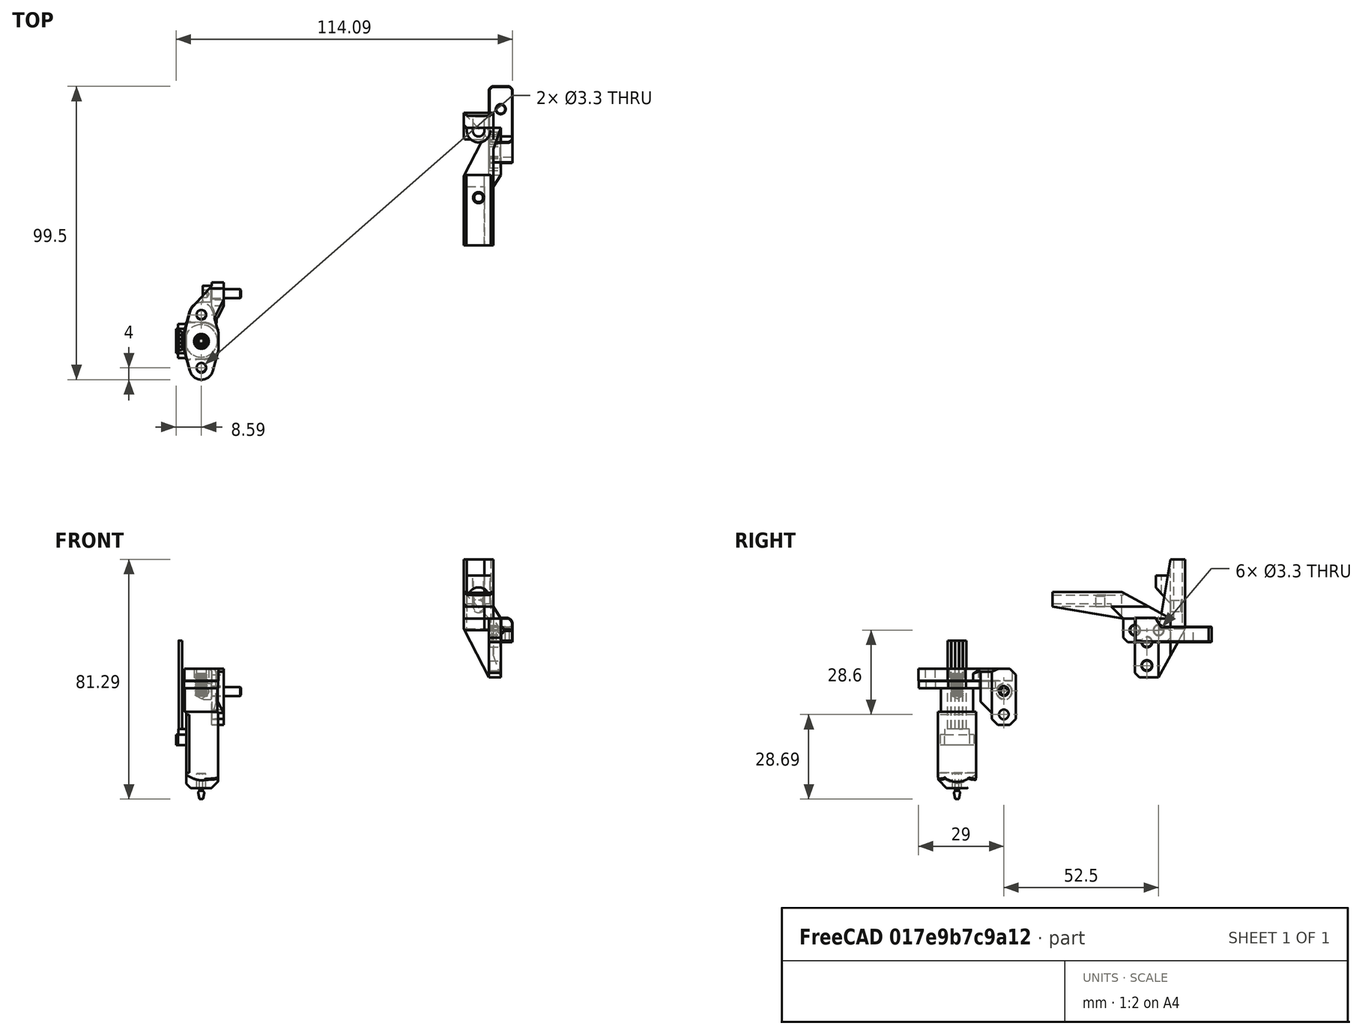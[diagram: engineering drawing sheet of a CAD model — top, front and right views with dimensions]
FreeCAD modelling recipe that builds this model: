
FCSTD DOCUMENT  (FreeCAD 0.19R24291 (Git))
Label: probe-mount-GXH8B
License: Other
LicenseURL: GPL3
objects: Part::Chamfer×18, Part::Box×14, Part::Cut×11, Part::Cylinder×5, Part::MultiFuse×5, Part::Feature×4, Part::FeaturePython×2, Part::Fillet×1, App::Part×1, Part::Refine×1
note: 61 computed .brp shape members not serialized (recipe doc carries the construction recipe); baked Part::Feature solids carry a one-line shape summary decoded from their .brp

FEATURE [Part::Box] Box  label="Cube"
  AttacherType = Attacher::AttachEngine3D
  Height = 8.2
  Length = 8
  Width = 9
FEATURE [Part::Box] Box001  label="Cube001"
  AttacherType = Attacher::AttachEngine3D
  Height = 5.2
  Length = 8
  Placement = pos=(0,8,0) rot=(0,0,1;0rad)
  Width = 18
FEATURE [Part::Box] Box002  label="Cube002"
  AttacherType = Attacher::AttachEngine3D
  Height = 0.2
  Length = 8
  Width = 2
FEATURE [Part::Cylinder] Cylinder
  Angle = 360
  AttacherType = Attacher::AttachEngine3D
  Height = 10
  Placement = pos=(4,18.25,0) rot=(0,0,1;0rad)
  Radius = 1.5
FEATURE [Part::Cylinder] Cylinder001
  Angle = 360
  AttacherType = Attacher::AttachEngine3D
  Height = 10
  Placement = pos=(4,0.25,4) rot=(1,0,0;1.5708rad)
  Radius = 1
FEATURE [Part::Box] Box003  label="Cube003"
  AttacherType = Attacher::AttachEngine3D
  Height = 2
  Length = 0.4
  Placement = pos=(3.8,0,0.5) rot=(0,0,1;0rad)
  Width = 0.25
FEATURE [Part::Box] Box004  label="Cube004"
  AttacherType = Attacher::AttachEngine3D
  Height = 2
  Length = 0.4
  Placement = pos=(3.8,0,5.5) rot=(0,0,1;0rad)
  Width = 0.25
FEATURE [Part::MultiFuse] Fusion001
  Shapes = -> [Box003,Box004]
FEATURE [Part::Feature] Fusion001001
  Placement = pos=(-1.8e-15,0,8) rot=(0,1,0;1.5708rad)
  shape: bbox 7 x 0.25 x 0.4 mm, 12 faces, 2 solids (baked)
FEATURE [Part::MultiFuse] Fusion001002
  Shapes = -> [Fusion001,Fusion001001]
FEATURE [Part::Cylinder] Cylinder002
  Angle = 360
  AttacherType = Attacher::AttachEngine3D
  Height = 10
  Placement = pos=(-1e-15,0,4) rot=(0,1,0;1.5708rad)
  Radius = 1.65
FEATURE [Part::Cylinder] Cylinder003
  Angle = 360
  AttacherType = Attacher::AttachEngine3D
  Height = 10
  Placement = pos=(-1e-15,8,4) rot=(0,1,0;1.5708rad)
  Radius = 1.65
FEATURE [Part::Box] Box007  label="Cube007"
  AttacherType = Attacher::AttachEngine3D
  Height = 8
  Length = 4
  Placement = pos=(0,-4,0) rot=(0,0,1;0rad)
  Width = 16
FEATURE [Part::Box] Box008  label="Cube008"
  AttacherType = Attacher::AttachEngine3D
  Height = 9
  Length = 12.5
  Placement = pos=(-8.5,-8,8) rot=(0,0,1;0rad)
  Width = 20
FEATURE [Part::Box] Box009  label="Cube009"
  AttacherType = Attacher::AttachEngine3D
  Height = 5
  Length = 10
  Placement = pos=(-8.5,-28,12) rot=(0,0,1;0rad)
  Width = 23.5
FEATURE [Part::Box] Box010  label="Cube010"
  AttacherType = Attacher::AttachEngine3D
  Height = 10
  Length = 12.5
  Placement = pos=(1.5,-9.5,8) rot=(0,0,1;0rad)
  Width = 21.5
FEATURE [Part::Chamfer] Chamfer009
  Base = -> Box010
  Edges = 1 edges: [Edge4 r1=4 r2=2.5]
FEATURE [Part::Chamfer] Chamfer010
  Base = -> Box008
  Edges = 1 edges r=4: [Edge9]
FEATURE [Part::Cut] Cut003001002
  Base = -> Chamfer010
  Tool = -> Chamfer009
FEATURE [Part::Chamfer] Chamfer011
  Base = -> Box007
  Edges = 2 edges r=1.5: [Edge9,Edge11]
FEATURE [Part::MultiFuse] Fusion001003
  Shapes = -> [Cylinder003,Cylinder002]
FEATURE [Part::Cut] Cut003001003
  Base = -> Chamfer011
  Tool = -> Fusion001003
FEATURE [Part::Box] Box011  label="Cube011"
  AttacherType = Attacher::AttachEngine3D
  Height = 5
  Length = 8.2
  Placement = pos=(-7.6,-28.5,16) rot=(0,0,1;0rad)
  Width = 24
FEATURE [Part::Chamfer] Chamfer012
  Base = -> Cut003001002
  Edges = 1 edges: [Edge4 r1=16.5 r2=8.5]
FEATURE [Part::Box] Box012  label="Cube012"
  AttacherType = Attacher::AttachEngine3D
  Height = 17
  Length = 15
  Placement = pos=(-10.8,-4.5,8) rot=(0,0,1;0rad)
  Width = 21
FEATURE [Part::Chamfer] Chamfer013
  Base = -> Box012
  Edges = 1 edges: [Edge9 r1=9 r2=16.5]
FEATURE [Part::Cut] Cut003001004
  Base = -> Chamfer012
  Tool = -> Chamfer013
FEATURE [Part::Box] Box013  label="Cube013"
  AttacherType = Attacher::AttachEngine3D
  Height = 5
  Length = 3
  Placement = pos=(-1.5,-3.5,13) rot=(1,0,0;3.14159rad)
  Width = 24.5
FEATURE [Part::Cylinder] Cylinder004
  Angle = 360
  AttacherType = Attacher::AttachEngine3D
  Height = 10
  Placement = pos=(-3.5,-12.25,10) rot=(0,0,1;0rad)
  Radius = 1.9
FEATURE [Part::Cut] Cut
  Base = -> Box
  Tool = -> Box002
FEATURE [Part::Chamfer] Chamfer
  Base = -> Cut
  Edges = 1 edges: [Edge10 r1=2 r2=3]
FEATURE [Part::Fillet] Fillet
  Base = -> Chamfer
  Edges = 2 edges r=2: [Edge1,Edge9]
FEATURE [Part::Chamfer] Chamfer001
  Base = -> Fillet
  Edges = 2 edges r=0.2: [Edge2,Edge16]
FEATURE [Part::Chamfer] Chamfer002
  Base = -> Chamfer001
  Edges = 2 edges r=0.2: [Edge5,Edge31]
FEATURE [Part::Cut] Cut001
  Base = -> Chamfer002
  Tool = -> Cylinder001
FEATURE [Part::Chamfer] Chamfer005
  Base = -> Cut001
  Edges = 9 edges r=0.2: [Edge4,Edge17,Edge19,Edge20,Edge21,Edge22,Edge23,Edge24,Edge25]
FEATURE [Part::Chamfer] Chamfer006
  Base = -> Chamfer005
  Edges = 5 edges r=0.2: [Edge7,Edge9,Edge14,Edge15,Edge16]
FEATURE [Part::Cut] Cut003001008
  Base = -> Chamfer006
  Tool = -> Fusion001002
FEATURE [Part::Feature] Part__Feature112001139  label="BL-touch v3.x002"
  Placement = pos=(-97.5942,-60.3565,-13.2887) rot=(0,0,1;1.5708rad)
  shape: bbox 16.53 x 26.01 x 53.81 mm, 111 faces (baked)
FEATURE [Part::FeaturePython] Screw1371  label="M3x10-Screw189"  # Fasteners workbench fastener (typed FeaturePython)
  Placement = pos=(-94.0942,-44.3565,-16.7887) rot=(0,-1,0;1.5708rad)
  diameter = 4
  invert = false
  leftHanded = false
  length = 10
  lengthCustom = 10
  matchOuter = true
  offset = 0
  thread = false
  type = 33
FEATURE [Part::Feature] Part__Feature  label="bltouch-mount"
  Placement = pos=(-69.5,-39.5,-13.1) rot=(0,0,1;0rad)
  shape: bbox 13.25 x 33 x 19 mm, 31 faces (baked)
FEATURE [App::Part] BL_Touch__1_001  label="BL-Touch <1>001"
  Group = -> [Part__Feature112001139,Screw1371,Part__Feature]
  Origin = -> Origin206
  Placement = pos=(70,24.5,-40.5) rot=(1,0,0;4.71239rad)
FEATURE [Part::Chamfer] Chamfer021
  Base = -> Box001
  Edges = 2 edges r=1: [Edge3,Edge7]
FEATURE [Part::Chamfer] Chamfer022
  Base = -> Chamfer021
  Edges = 12 edges r=0.2: [Edge1,Edge3,Edge5,Edge6,Edge7,Edge8,Edge9,Edge10,Edge12,Edge14,Edge15,Edge16]
FEATURE [Part::MultiFuse] Fusion
  Shapes = -> [Chamfer022,Cut003001008]
FEATURE [Part::Chamfer] Chamfer023003
  Base = -> Box009
  Edges = 2 edges r=1: [Edge4,Edge8]
FEATURE [Part::Chamfer] Chamfer023004
  Base = -> Box013
  Edges = 1 edges: [Edge12 r1=4 r2=24]
FEATURE [Part::MultiFuse] Fusion001004
  Shapes = -> [Cut003001003,Cut003001004,Chamfer023004,Chamfer023003]
FEATURE [Part::Cut] Cut003001014
  Base = -> Fusion
  Refine = true
  Tool = -> Cylinder
FEATURE [Part::Chamfer] Chamfer023007
  Base = -> Cut003001014
  Edges = 2 edges r=0.2: [Edge70,Edge133]
FEATURE [Part::Feature] Chamfer023006001  label="old"
  shape: bbox 12.5 x 40 x 17 mm, 46 faces (baked)
FEATURE [Part::Cut] Cut003001015
  Base = -> Fusion001004
  Tool = -> Box011
FEATURE [Part::Cut] Cut003001016
  Base = -> Cut003001015
  Tool = -> Cylinder004
FEATURE [Part::Chamfer] Chamfer023006002
  Base = -> Cut003001016
  Edges = 1 edges r=0.4: [Edge92]
FEATURE [Part::Chamfer] Chamfer023006003
  Base = -> Chamfer023006002
  Edges = 4 edges r=0.2: [Edge73,Edge74,Edge96,Edge98]
FEATURE [Part::Refine] Chamfer023006003001
  Placement = pos=(0,0,0) rot=(-1,0,0;1.5708rad)
  Source = -> Chamfer023006003
FEATURE [Part::FeaturePython] Tube  # WARN: FeaturePython — macro-defined, semantics opaque (R4)
  AttacherType = Attacher::AttachEngine3D
  Height = 10
  InnerRadius = 2
  OuterRadius = 4
  Placement = pos=(-3.5,11,12) rot=(0,0,1;0rad)
FEATURE [Part::Box] Box014  label="Cube014"
  AttacherType = Attacher::AttachEngine3D
  Height = 19
  Length = 10
  Placement = pos=(-10.5,0,0) rot=(0,0,1;0rad)
  Width = 10
FEATURE [Part::Chamfer] Chamfer023006003002
  Base = -> Box014
  Edges = 1 edges: [Edge12 r1=10 r2=9]
  Placement = pos=(2,2,3.5) rot=(0,0,1;0rad)
FEATURE [Part::Cut] Cut003001017
  Base = -> Tube
  Tool = -> Chamfer023006003002
FEATURE [Part::Box] Box015  label="Cube015"
  AttacherType = Attacher::AttachEngine3D
  Height = 19
  Length = 10
  Placement = pos=(-8.5,12,8.5) rot=(0,0,1;0rad)
  Width = 10
FEATURE [Part::Cut] Cut003001018
  Base = -> Cut003001017
  Placement = pos=(0,0,0.5) rot=(0,0,1;0rad)
  Tool = -> Box015
